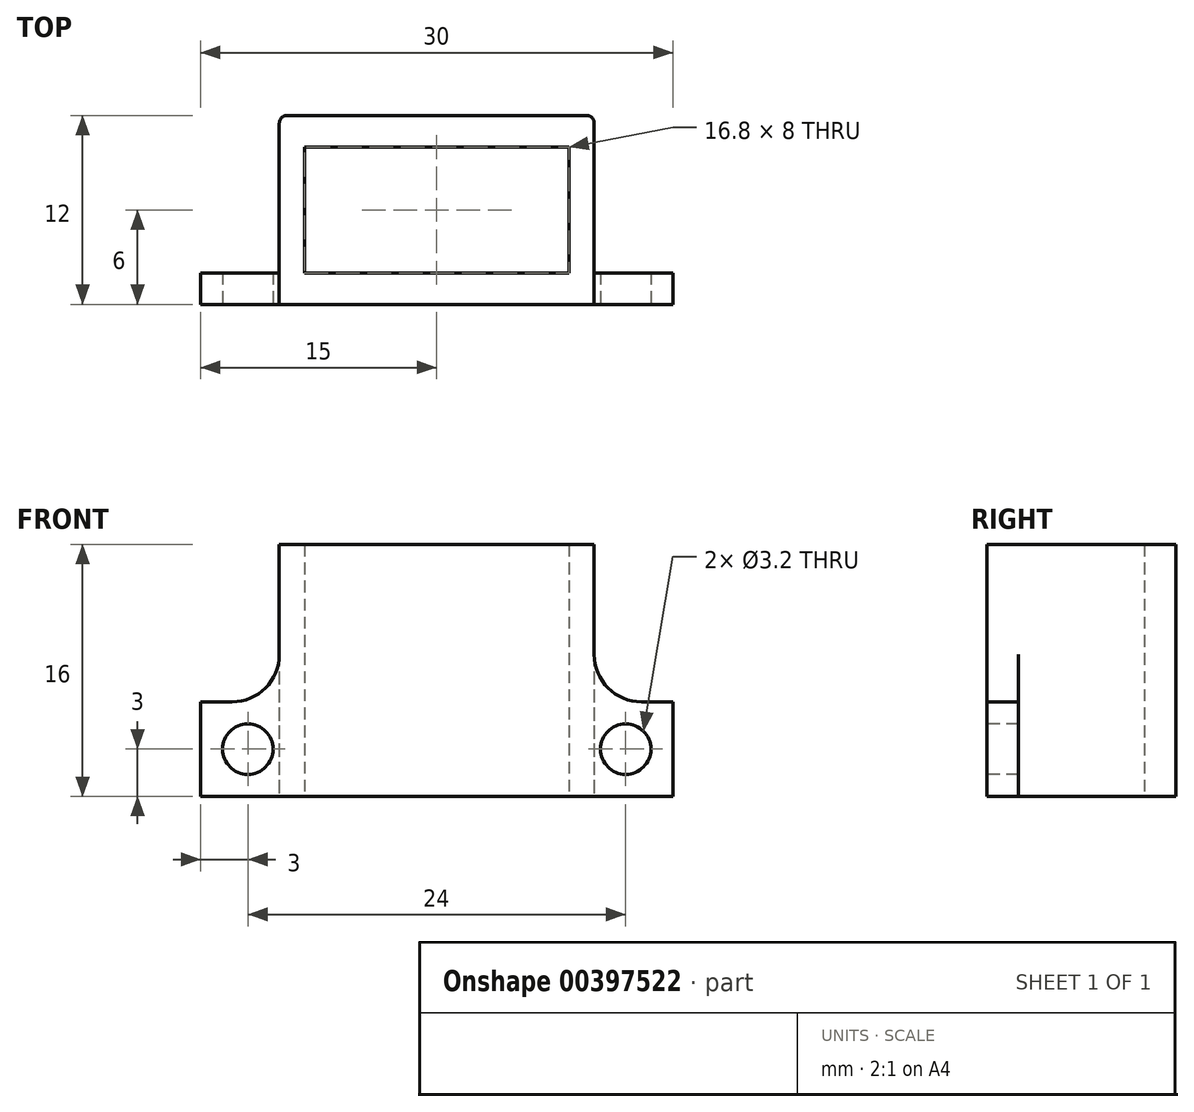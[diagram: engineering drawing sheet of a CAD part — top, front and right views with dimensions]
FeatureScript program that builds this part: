
annotation { "Feature Type Name" : "Feature", "Feature Type Description" : "" }
export const myFeature = defineFeature(function(context is Context, id is Id, definition is map)
    precondition{}
    {
        {
            var Q0;
            Q0=qCreatedBy(makeId("Top.planeOp"),FACE);
            var sketch = newSketch(context, id + "F0", { "sketchPlane" : qUnion([Q0])});
            skLineSegment(sketch, "E0.bottom", {"start": v(-15, 0) * mm, "end": v(15, 0) * mm});
            skLineSegment(sketch, "E0.top", {"start": v(-15, 2) * mm, "end": v(-10, 2) * mm});
            skLineSegment(sketch, "E0.left", {"start": v(-15, 0) * mm, "end": v(-15, 2) * mm});
            skLineSegment(sketch, "E0.right", {"start": v(15, 0) * mm, "end": v(15, 2) * mm});
            skLineSegment(sketch, "E1.top", {"start": v(-8.4, 10) * mm, "end": v(8.4, 10) * mm});
            skLineSegment(sketch, "E1.left", {"start": v(-8.4, 2) * mm, "end": v(-8.4, 10) * mm});
            skLineSegment(sketch, "E1.right", {"start": v(8.4, 2) * mm, "end": v(8.4, 10) * mm});
            skLineSegment(sketch, "E2", {"start": v(-10, 2) * mm, "end": v(-10, 11.5) * mm});
            skLineSegment(sketch, "E3", {"start": v(-9.5, 12) * mm, "end": v(9.5, 12) * mm});
            skLineSegment(sketch, "E4", {"start": v(10, 11.5) * mm, "end": v(10, 2) * mm});
            skPoint(sketch, "E5.visualSharp", {"position": v(-10, 12) * mm});
            skArc(sketch, "E5.filletArc", {"start": v(-9.5, 12) * mm, "mid": v(-9.85, 11.85) * mm, "end": v(-10, 11.5) * mm});
            skPoint(sketch, "E6.visualSharp", {"position": v(10, 12) * mm});
            skArc(sketch, "E6.filletArc", {"start": v(10, 11.5) * mm, "mid": v(9.85, 11.85) * mm, "end": v(9.5, 12) * mm});
            skLineSegment(sketch, "E7.trimOffspring", {"start": v(-8.4, 2) * mm, "end": v(8.4, 2) * mm});
            skLineSegment(sketch, "E8.trimOffspring", {"start": v(10, 2) * mm, "end": v(15, 2) * mm});
            skSolve(sketch);
        }
        {
            var Q0;
            Q0 = qSketchRegion(id + "F0", true);
            extrude(context, id + "F1", {"entities" : qUnion([Q0]), "depth" : 16 * mm});
        }
        {
            var Q0;
            Q0=makeQuery(id+"F1.opExtrude","SWEPT_FACE",FACE,{"disambiguationData":[OSD([sQuery(id+"F0.wireOp",EDGE,"E0.bottom")])]});
            var sketch = newSketch(context, id + "F2", { "sketchPlane" : qUnion([Q0])});
            skCircle(sketch, "E9", {"center": v(-12, 3) * mm, "radius": 1.6 * mm});
            skCircle(sketch, "E10.MirrorC", {"center": v(12, 3) * mm, "radius": 1.6 * mm});
            skLineSegment(sketch, "E11.bottom", {"start": v(-15, 16) * mm, "end": v(-10, 16) * mm});
            skLineSegment(sketch, "E11.top", {"start": v(-15, 6) * mm, "end": v(-13, 6) * mm});
            skLineSegment(sketch, "E11.left", {"start": v(-15, 16) * mm, "end": v(-15, 6) * mm});
            skLineSegment(sketch, "E11.right", {"start": v(-10, 16) * mm, "end": v(-10, 9) * mm});
            skLineSegment(sketch, "E12.bottom", {"start": v(15, 16) * mm, "end": v(10, 16) * mm});
            skLineSegment(sketch, "E12.top", {"start": v(15, 6) * mm, "end": v(13, 6) * mm});
            skLineSegment(sketch, "E12.left", {"start": v(15, 16) * mm, "end": v(15, 6) * mm});
            skLineSegment(sketch, "E12.right", {"start": v(10, 16) * mm, "end": v(10, 9) * mm});
            skPoint(sketch, "E13.visualSharp", {"position": v(-10, 6) * mm});
            skArc(sketch, "E13.filletArc", {"start": v(-13, 6) * mm, "mid": v(-10.88, 6.88) * mm, "end": v(-10, 9) * mm});
            skPoint(sketch, "E14.visualSharp", {"position": v(10, 6) * mm});
            skArc(sketch, "E14.filletArc", {"start": v(10, 9) * mm, "mid": v(10.88, 6.88) * mm, "end": v(13, 6) * mm});
            skSolve(sketch);
        }
        {
            var Q0;
            Q0 = qSketchRegion(id + "F2", true);
            extrude(context, id + "F3", {"entities" : qUnion([Q0]), "operationType" : NewBodyOperationType.REMOVE, "oppositeDirection" : true, "depth" : 25 * mm});
        }
    });
